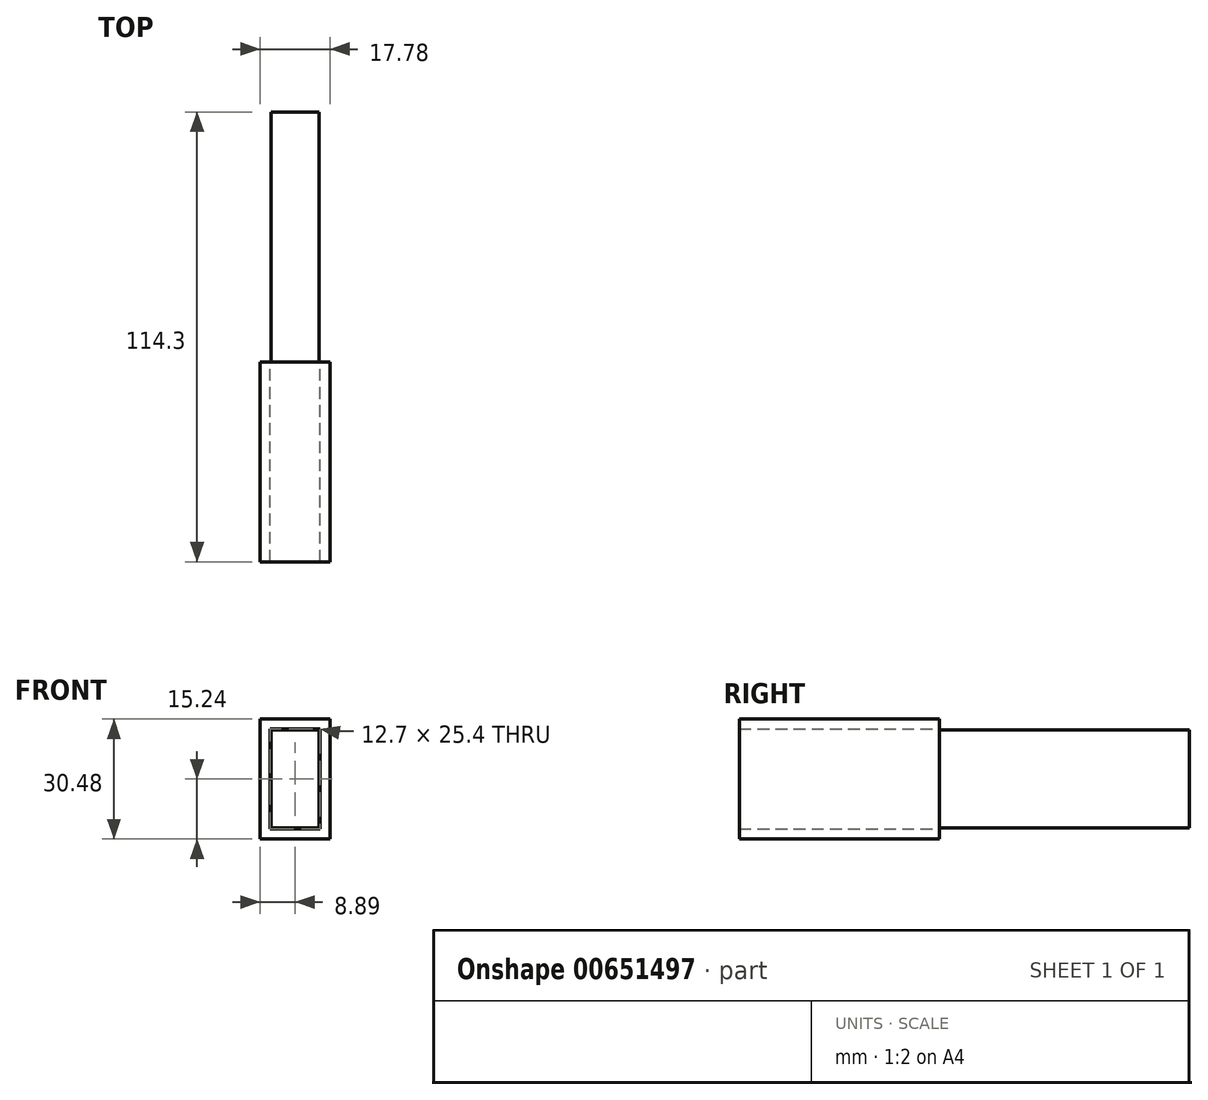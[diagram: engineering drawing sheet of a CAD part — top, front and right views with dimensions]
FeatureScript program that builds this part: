
annotation { "Feature Type Name" : "Feature", "Feature Type Description" : "" }
export const myFeature = defineFeature(function(context is Context, id is Id, definition is map)
    precondition{}
    {
        {
            var Q0;
            Q0=qCreatedBy(makeId("Front.planeOp"),FACE);
            var sketch = newSketch(context, id + "F0", { "sketchPlane" : qUnion([Q0])});
            skLineSegment(sketch, "E0.bottom", {"start": v(0, 0) * mm, "end": v(12.7, 0) * mm});
            skLineSegment(sketch, "E0.top", {"start": v(0, 25.4) * mm, "end": v(12.7, 25.4) * mm});
            skLineSegment(sketch, "E0.left", {"start": v(0, 0) * mm, "end": v(0, 25.4) * mm});
            skLineSegment(sketch, "E0.right", {"start": v(12.7, 0) * mm, "end": v(12.7, 25.4) * mm});
            skLineSegment(sketch, "E1", {"start": v(6.35, 0) * mm, "end": v(6.35, -2.54) * mm, "construction": true});
            skLineSegment(sketch, "E2", {"start": v(12.7, 12.7) * mm, "end": v(15.24, 12.7) * mm, "construction": true});
            skLineSegment(sketch, "E3", {"start": v(6.35, 25.4) * mm, "end": v(6.35, 27.94) * mm, "construction": true});
            skLineSegment(sketch, "E4", {"start": v(0, 12.7) * mm, "end": v(-2.54, 12.7) * mm, "construction": true});
            skLineSegment(sketch, "E5", {"start": v(-2.54, 12.7) * mm, "end": v(-2.54, 27.94) * mm, "construction": true});
            skLineSegment(sketch, "E6", {"start": v(6.35, -2.54) * mm, "end": v(15.24, -2.54) * mm, "construction": true});
            skLineSegment(sketch, "E7", {"start": v(15.24, 12.7) * mm, "end": v(15.24, -2.54) * mm, "construction": true});
            skLineSegment(sketch, "E8.bottom", {"start": v(-2.54, 27.94) * mm, "end": v(15.24, 27.94) * mm});
            skLineSegment(sketch, "E8.top", {"start": v(-2.54, -2.54) * mm, "end": v(15.24, -2.54) * mm});
            skLineSegment(sketch, "E8.left", {"start": v(-2.54, 27.94) * mm, "end": v(-2.54, -2.54) * mm});
            skLineSegment(sketch, "E8.right", {"start": v(15.24, 27.94) * mm, "end": v(15.24, -2.54) * mm});
            skSolve(sketch);
        }
        {
            var Q0;
            Q0=makeQuery(id+"F0.imprint","IMPRINT",FACE,{"disambiguationData":[TD([[makeQuery(id+"F0.imprint","IMPRINT",EDGE,{"derivedFrom":sQuery(id+"F0.wireOp",EDGE,"E0.bottom")}),-1.0]])]});
            extrude(context, id + "F1", {"entities" : qUnion([Q0]), "depth" : 50.8 * mm, "offsetDistance" : 25.4 * mm});
        }
        {
            var Q0;
            Q0=makeQuery(id+"F1.opExtrude","CAP_FACE",FACE,{"disambiguationData":[OSD([sQuery(id+"F0.wireOp",EDGE,"E0.bottom"),sQuery(id+"F0.wireOp",EDGE,"E0.top"),sQuery(id+"F0.wireOp",EDGE,"E0.left"),sQuery(id+"F0.wireOp",EDGE,"E0.right"),sQuery(id+"F0.wireOp",EDGE,"E8.bottom"),sQuery(id+"F0.wireOp",EDGE,"E8.top"),sQuery(id+"F0.wireOp",EDGE,"E8.left"),sQuery(id+"F0.wireOp",EDGE,"E8.right")])],"isStart":true});
            var sketch = newSketch(context, id + "F2", { "sketchPlane" : qUnion([Q0])});
            skLineSegment(sketch, "E9", {"start": v(-6.35, 25.4) * mm, "end": v(-6.35, 0) * mm, "construction": true});
            skLineSegment(sketch, "E10", {"start": v(-12.7, 12.7) * mm, "end": v(0, 12.7) * mm, "construction": true});
            skLineSegment(sketch, "E11.bottom", {"start": v(-0.25, 25.15) * mm, "end": v(-12.45, 25.15) * mm});
            skLineSegment(sketch, "E11.top", {"start": v(-0.25, 0.25) * mm, "end": v(-12.45, 0.25) * mm});
            skLineSegment(sketch, "E11.left", {"start": v(-0.25, 25.15) * mm, "end": v(-0.25, 0.25) * mm});
            skLineSegment(sketch, "E11.right", {"start": v(-12.45, 25.15) * mm, "end": v(-12.45, 0.25) * mm});
            skPoint(sketch, "E11.middle", {"position": v(-6.35, 12.7) * mm});
            skSolve(sketch);
        }
        {
            var Q0;
            Q0=makeQuery(id+"F2.imprint","IMPRINT",FACE,{"disambiguationData":[TD([[makeQuery(id+"F2.imprint","IMPRINT",EDGE,{"derivedFrom":sQuery(id+"F2.wireOp",EDGE,"E11.bottom")}),1.0]])]});
            extrude(context, id + "F3", {"entities" : qUnion([Q0]), "depth" : 63.5 * mm, "offsetDistance" : 25.4 * mm});
        }
    });
